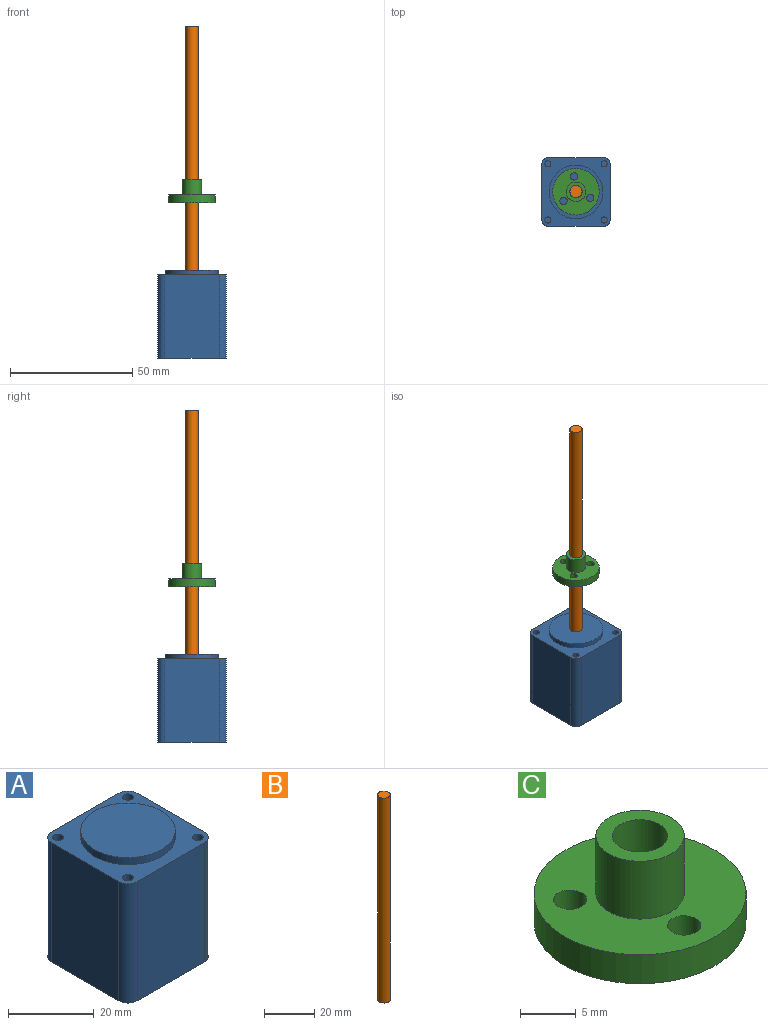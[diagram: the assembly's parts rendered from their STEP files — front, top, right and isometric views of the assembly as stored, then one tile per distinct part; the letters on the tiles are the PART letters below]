
ASSEMBLY  parts=3 mates=2
PART A: 20 faces, bbox 28.2x28.2x36 mm
  f0: plane 28.2x28.2mm, normal (0,0,1), area 387.7mm2, adj f1,f3,f4,f5,f6,f8,f10,f12
  f1: plane 34x22.2mm, normal (-1,0,0), area 754.8mm2, adj f0,f2,f17,f19
  f2: plane 28.2x28.2mm, normal (0,0,-1), area 787.5mm2, adj f1,f3,f4,f5,f16,f17,f18,f19
  f3: plane 34x22.2mm, normal (1,0,0), area 754.8mm2, adj f0,f2,f16,f18
  f4: plane 34x22.2mm, normal (0,-1,0), area 754.8mm2, adj f0,f2,f18,f19
  f5: plane 34x22.2mm, normal (0,1,0), area 754.8mm2, adj f0,f2,f16,f17
  f6: cylinder r=1.25mm len=3.5mm, axis (0,0,1), area 27.5mm2, adj f0,f7
  f7: plane 2.5x2.5mm, normal (0,0,1), area 4.9mm2, adj f6
  f8: cylinder r=1.25mm len=3.5mm, axis (0,0,1), area 27.5mm2, adj f0,f9
  f9: plane 2.5x2.5mm, normal (0,0,1), area 4.9mm2, adj f8
  f10: cylinder r=1.25mm len=3.5mm, axis (0,0,1), area 27.5mm2, adj f0,f11
  f11: plane 2.5x2.5mm, normal (0,0,1), area 4.9mm2, adj f10
  f12: cylinder r=1.25mm len=3.5mm, axis (0,0,1), area 27.5mm2, adj f0,f13
  f13: plane 2.5x2.5mm, normal (0,0,1), area 4.9mm2, adj f12
  f14: cylinder r=11mm len=22mm, axis (0,0,-1), area 138.2mm2, adj f0,f15
  f15: plane 22x22mm, normal (0,0,1), area 380.1mm2, adj f14
  f16: cylinder r=3mm len=34mm, axis (0,0,1), area 160.2mm2, adj f0,f2,f3,f5
  f17: cylinder r=3mm len=34mm, axis (0,0,-1), area 160.2mm2, adj f0,f1,f2,f5
  f18: cylinder r=3mm len=34mm, axis (0,0,-1), area 160.2mm2, adj f0,f2,f3,f4
  f19: cylinder r=3mm len=34mm, axis (0,0,1), area 160.2mm2, adj f0,f1,f2,f4
PART B: 3 faces, bbox 5x5x100 mm
  f0: cylinder r=2.5mm len=100mm, axis (0,0,-1), area 1570.8mm2, adj f1,f2
  f1: plane 5x5mm, normal (0,0,1), area 19.6mm2, adj f0
  f2: plane 5x5mm, normal (0,0,-1), area 19.6mm2, adj f0
PART C: 9 faces, bbox 19.1x19.1x9.5 mm
  f0: cylinder r=2.5mm len=9.53mm, axis (0,0,-1), area 149.7mm2, adj f3,f5
  f1: cylinder r=9.53mm len=19.05mm, axis (0,0,-1), area 190.3mm2, adj f2,f3
  f2: plane 19.05x19.05mm, normal (0,0,1), area 214.3mm2, adj f1,f4,f6,f7,f8
  f3: plane 19.05x19.05mm, normal (0,0,-1), area 244.2mm2, adj f0,f1,f6,f7,f8
  f4: cylinder r=3.97mm len=7.94mm, axis (0,0,-1), area 158.4mm2, adj f2,f5
  f5: plane 7.94x7.94mm, normal (0,0,1), area 29.9mm2, adj f0,f4
  f6: cylinder r=1.5mm len=3.18mm, axis (0,0,-1), area 30mm2, adj f2,f3
  f7: cylinder r=1.5mm len=3.18mm, axis (0,0,-1), area 30mm2, adj f2,f3
  f8: cylinder r=1.5mm len=3.18mm, axis (0,0,-1), area 30mm2, adj f2,f3
PLACE A at identity fixed
PLACE B t=(0,0,2)mm
PLACE C rot(axis=(0,0,-1),167.2deg) t=(0,0,27.63)mm
MATE fastened B.f0 <-> A.f14  axis (0,0,-1) through (0,0,2)mm
MATE cylindrical C.f0 <-> A.f14  axis (0,0,1) through (0,0,29.63)mm
